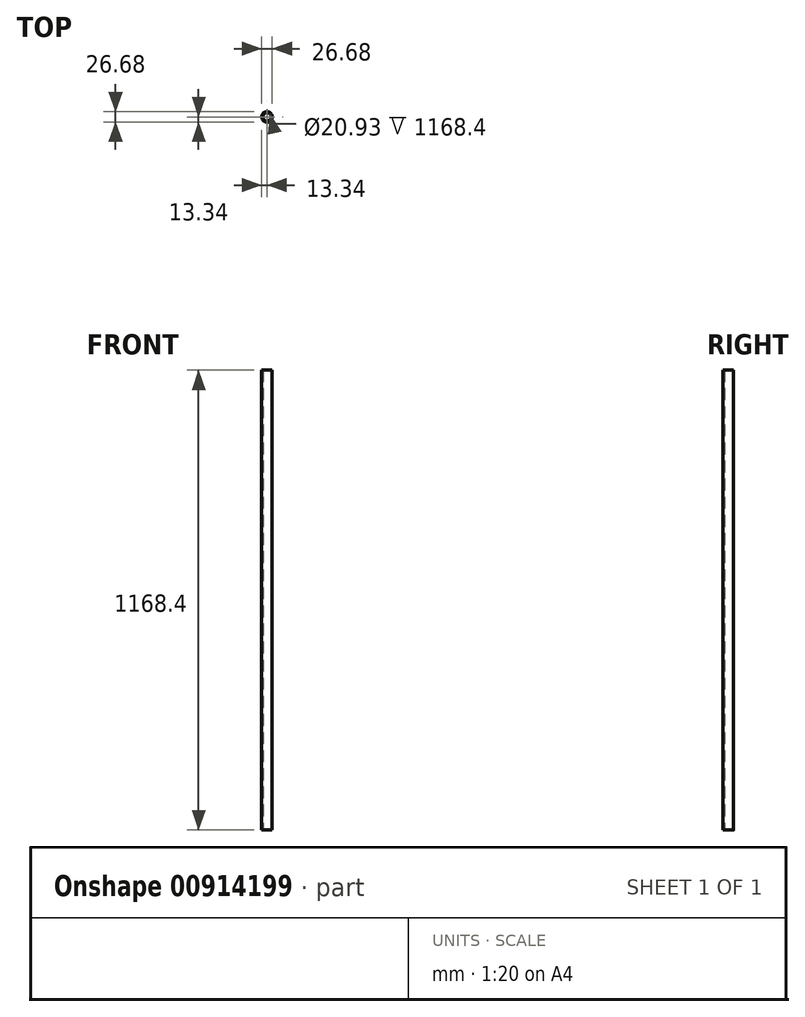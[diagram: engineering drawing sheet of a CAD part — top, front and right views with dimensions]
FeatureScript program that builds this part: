
annotation { "Feature Type Name" : "Feature", "Feature Type Description" : "" }
export const myFeature = defineFeature(function(context is Context, id is Id, definition is map)
    precondition{}
    {
        {
            var Q0;
            Q0=qCreatedBy(makeId("Top.planeOp"),FACE);
            var sketch = newSketch(context, id + "F0", { "sketchPlane" : qUnion([Q0])});
            skCircle(sketch, "E0", {"center": v(0, 0) * mm, "radius": 13.34 * mm});
            skCircle(sketch, "E1", {"center": v(0, 0) * mm, "radius": 10.46 * mm});
            skSolve(sketch);
        }
        {
            var Q0;
            Q0=qSketchRegion(id+"F0",true);
            extrude(context, id + "F1", {"entities" : qUnion([Q0]), "depth" : 1168.4 * mm, "offsetDistance" : 25.4 * mm});
        }
    });
